# Revit family: 2093186 Sylvania Lighting Fixture CURVELYTE 1265 HO LG D I 3K DALI BLACK
name_source: partatom
category: Lighting Fixtures
revit_build: Autodesk Revit 2016 (Build: 20150220_1215(x64)
units: mm (PartAtom-declared; Revit-internal decimal feet)

## family parameters
Cut with Voids When Loaded = No
Host = Face
Light Source = Yes
OmniClass Number = 23.80.70.00
OmniClass Title = Lighting
Part Type = Normal
Room Calculation Point = No
Round Connector Dimension = Use Diameter
Shared = No

## types (1)
- 2093175 CURVELYTE 1265 HO D/I 3K DALI BLACK
    Apparent Load = 55 VA
    Assembly Code = D5020200
    AssetType = Fixed
    ClassificationName = Uniclass2015
    ClassificationValue = EF_70_80
    Color Filter = 16777215
    Cost = 0 $
    Default Elevation = 1219 mm
    Description = CURVELYTE 1265x330 HO D/I 3K DALI BLACK is a suspended LED Linear luminaire with Direct / Indirect (70/30) distribution. Luminaire Dimensions: 1265x336x46mm, Black body colour, IP20, IK06. Constant Current, Low LED flicker (<5%), Warm White (3000K) LED Colour Temperature, 6250lm, 55W, 114lm/W efficacy, CRI>80, 3 SDCM (3-step MacAdam ellipse) LED Colour Consistency, Lumen Maintenance: L90B10 at 50,000 hours, Terminal block connection in the driver box. Glow Wire Test 650°C.
    Dimming Lamp Color Temperature Shift = <None>
    DocumentationLiterature = http://www.sylvania-lighting.com
    DurationUnit = hours
    ElectricShockClassification = Class I
    Emit Shape Visible in Rendering = No
    Emit from Rectangle Length = 1188 mm  [stored 3.89764 ft]
    Emit from Rectangle Width = 280 mm  [stored 0.918635 ft]
    ExpectedLife = 50000
    IfcExportAs = IfcLightFixtureType
    IfcExportType = IfcLightFixtureType
    ImpactProtectionIndex = IK06
    IngressProtection = IP20
    InputNominalFrequency = 50/60 Hz
    Keynote = 16500
    Lamp = LED
    LampColourRenderingIndex = 80
    LampColourTemperature = 3000 K
    LampNominalLuminous = 6250 lm
    LampsType = LED
    LuminousEfficacy = 114 lm/W
    Manufacturer = Feilo Sylvania
    ManufacturerName = Feilo Sylvania
    Material_1_FEILO = <By Category>
    Material_2_FEILO = <By Category>
    Material_3_FEILO = <By Category>
    Material_4_FEILO = <By Category>
    Model = CURVELYTE 1265 HO D/I 3K DALI BLACK
    ModelNumber = 2093175
    ModelReference = CURVELYTE 1265 HO D/I 3K DALI BLACK
    Name = CURVELYTE 1265 HO D/I 3K DALI BLACK
    NominalDepth = 336 mm  [stored 1.10236 ft]
    NominalHeight = 46 mm  [stored 0.150919 ft]
    NominalLength = 1265 mm  [stored 4.15026 ft]
    Photometric Web File = 2093175.ies
    PowerConsumption = 55 W
    PowerFactor = 0
    Tilt Angle = -90.00°
    Type Image = <None>
    TypeName = CURVELYTE 1265 HO D/I 3K DALI BLACK
    URL = http://www.sylvania-lighting.com
    Voltage = 230 V
    Weight = 5.8 kg
    WireRad_SYL = 2 mm  [stored 0.00656168 ft]

note: [stored X ft] marks values corroborated as IEEE doubles in the binary element streams (Revit-internal decimal feet)

## geometry (parser evidence)
native form markers: Sweep x14
no freeform markers — native parametric forms only
